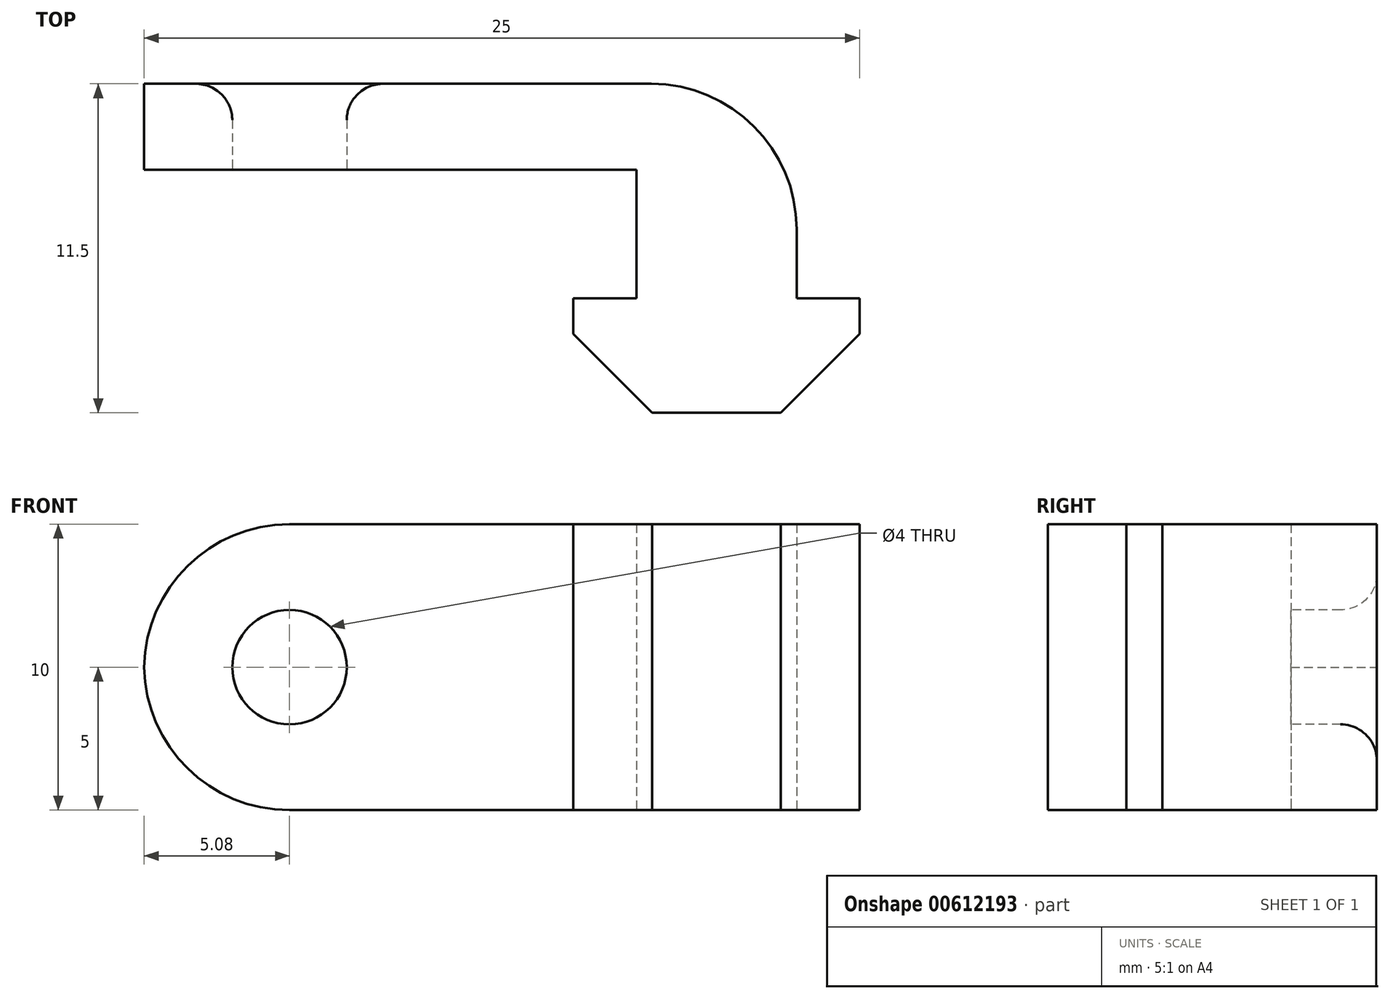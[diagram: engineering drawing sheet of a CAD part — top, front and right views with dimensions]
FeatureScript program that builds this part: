
annotation { "Feature Type Name" : "Feature", "Feature Type Description" : "" }
export const myFeature = defineFeature(function(context is Context, id is Id, definition is map)
    precondition{}
    {
        {
            var Q0;
            Q0=qCreatedBy(makeId("Top.planeOp"),FACE);
            var sketch = newSketch(context, id + "F0", { "sketchPlane" : qUnion([Q0])});
            skLineSegment(sketch, "E0", {"start": v(0, -4) * mm, "end": v(2.25, -4) * mm});
            skLineSegment(sketch, "E1", {"start": v(2.25, -4) * mm, "end": v(5, -1.25) * mm});
            skLineSegment(sketch, "E2", {"start": v(5, -1.25) * mm, "end": v(5, 0) * mm});
            skLineSegment(sketch, "E3", {"start": v(5, 0) * mm, "end": v(2.8, 0) * mm});
            skLineSegment(sketch, "E4", {"start": v(2.8, 0) * mm, "end": v(2.8, 4) * mm});
            skLineSegment(sketch, "E5.MirrorCS", {"start": v(-2.8, 0) * mm, "end": v(-2.8, 4) * mm});
            skLineSegment(sketch, "E6.MirrorCS", {"start": v(-5, 0) * mm, "end": v(-2.8, 0) * mm});
            skLineSegment(sketch, "E7.MirrorCS", {"start": v(-5, -1.25) * mm, "end": v(-5, 0) * mm});
            skLineSegment(sketch, "E8.MirrorCS", {"start": v(-2.25, -4) * mm, "end": v(-5, -1.25) * mm});
            skLineSegment(sketch, "E9.MirrorCS", {"start": v(0, -4) * mm, "end": v(-2.25, -4) * mm});
            skLineSegment(sketch, "E10", {"start": v(-2.8, 4) * mm, "end": v(-2.8, 4.5) * mm});
            skLineSegment(sketch, "E11", {"start": v(-2.8, 4.5) * mm, "end": v(-20, 4.5) * mm});
            skLineSegment(sketch, "E12", {"start": v(-20, 4.5) * mm, "end": v(-20, 7.5) * mm});
            skLineSegment(sketch, "E13", {"start": v(-20, 7.5) * mm, "end": v(2.8, 7.5) * mm});
            skLineSegment(sketch, "E14", {"start": v(2.8, 7.5) * mm, "end": v(2.8, 4) * mm});
            skSolve(sketch);
        }
        {
            var Q0;
            Q0=makeQuery(id+"F0.imprint","IMPRINT",FACE,{"disambiguationData":[TD([[makeQuery(id+"F0.imprint","IMPRINT",EDGE,{"derivedFrom":sQuery(id+"F0.wireOp",EDGE,"E0")}),1.0]])]});
            extrude(context, id + "F1", {"entities" : qUnion([Q0]), "depth" : 10 * mm, "offsetDistance" : 25.4 * mm});
        }
        {
            var Q0;
            Q0=makeQuery(id+"F1.opExtrude","SWEPT_EDGE",EDGE,{"disambiguationData":[OSD([sQuery(id+"F0.wireOp",EDGE,"E13"),sQuery(id+"F0.wireOp",EDGE,"E14")])]});
            fillet(context, id + "F2", {"entities" : qUnion([Q0]), "radius" : 5.08 * mm, "tangentPropagation" : true, "allowEdgeOverflow" : false});
        }
        {
            var Q0;
            Q0=makeQuery(id+"F1.opExtrude","CAP_EDGE",EDGE,{"disambiguationData":[OSD([sQuery(id+"F0.wireOp",EDGE,"E12")])],"isStart":false});
            var Q1;
            Q1=makeQuery(id+"F1.opExtrude","CAP_EDGE",EDGE,{"disambiguationData":[OSD([sQuery(id+"F0.wireOp",EDGE,"E12")])],"isStart":true});
            fillet(context, id + "F3", {"entities" : qUnion([Q0, Q1]), "radius" : 5.08 * mm, "tangentPropagation" : true, "allowEdgeOverflow" : false});
        }
        {
            var Q0;
            Q0=makeQuery(id+"F1.opExtrude","SWEPT_FACE",FACE,{"disambiguationData":[OSD([sQuery(id+"F0.wireOp",EDGE,"E11")])]});
            var sketch = newSketch(context, id + "F4", { "sketchPlane" : qUnion([Q0])});
            skCircle(sketch, "E15", {"center": v(-14.92, 5) * mm, "radius": 2 * mm});
            skSolve(sketch);
        }
        {
            var Q0;
            Q0 = qSketchRegion(id + "F4", true);
            extrude(context, id + "F5", {"entities" : qUnion([Q0]), "operationType" : NewBodyOperationType.REMOVE, "oppositeDirection" : true, "depth" : 25.4 * mm, "offsetDistance" : 25.4 * mm});
        }
        {
            var Q0;
            Q0=makeQuery(id+"F5.boolean.opBoolean","COPY",EDGE,{"derivedFrom":makeQuery(id+"F5.opExtrude","CAP_EDGE",EDGE,{"disambiguationData":[OSD([sQuery(id+"F4.wireOp",EDGE,"E15")])],"isStart":true})});
            var Q1;
            Q1=makeQuery(id+"F5.boolean.opBoolean","INTERSECT",EDGE,{"derivedFrom":[makeQuery(id+"F1.opExtrude","SWEPT_FACE",FACE,{"disambiguationData":[OSD([sQuery(id+"F0.wireOp",EDGE,"E13")])]}),makeQuery(id+"F5.opExtrude","SWEPT_FACE",FACE,{"disambiguationData":[OSD([sQuery(id+"F4.wireOp",EDGE,"E15")])]})]});
            fillet(context, id + "F6", {"entities" : qUnion([Q0, Q1]), "radius" : 1.27 * mm, "tangentPropagation" : true, "allowEdgeOverflow" : false});
        }
    });
